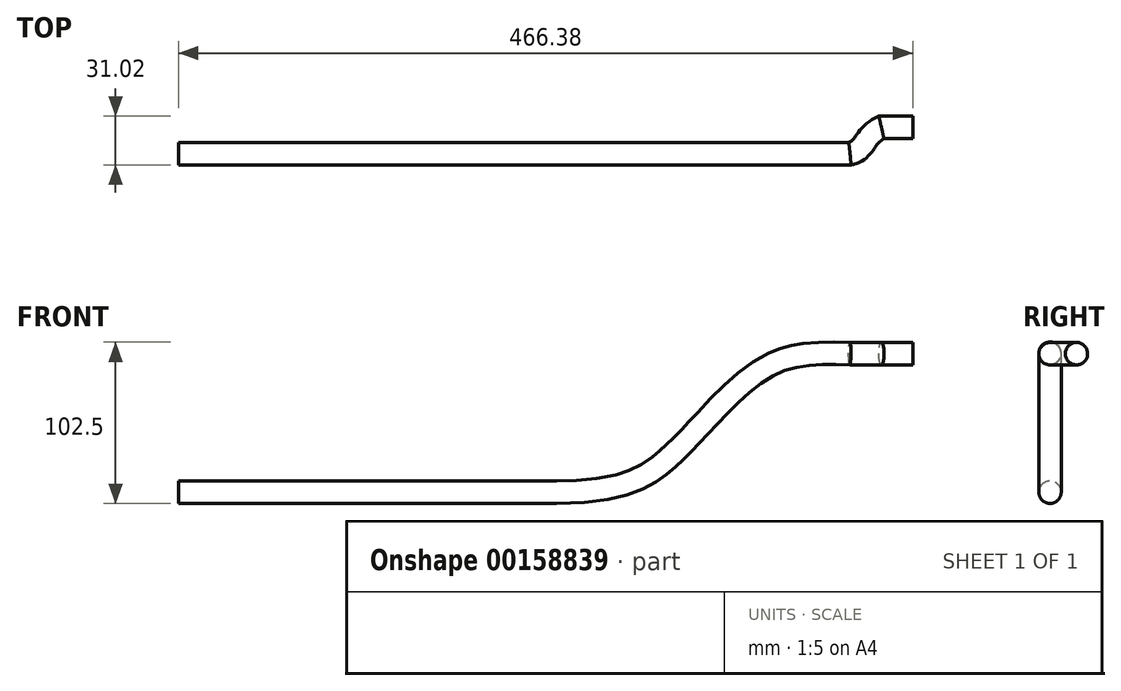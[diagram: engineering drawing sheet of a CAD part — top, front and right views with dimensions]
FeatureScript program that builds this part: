
annotation { "Feature Type Name" : "Feature", "Feature Type Description" : "" }
export const myFeature = defineFeature(function(context is Context, id is Id, definition is map)
    precondition{}
    {
        {
            var Q0;
            Q0=qCreatedBy(makeId("Top.planeOp"),FACE);
            var sketch = newSketch(context, id + "F0", { "sketchPlane" : qUnion([Q0])});
            skLineSegment(sketch, "E0", {"start": v(0, 0) * mm, "end": v(200, 0) * mm});
            skSolve(sketch);
        }
        {
            var Q0;
            Q0=qCreatedBy(makeId("Top.planeOp"),FACE);
            cPlane(context, id + "F1", {"entities" : qUnion([Q0]), "cplaneType" : CPlaneType.OFFSET, "offset" : 88.02 * mm, "width" : 150 * mm, "height" : 150 * mm});
        }
        {
            var Q0;
            Q0=qCreatedBy(makeId("Front.planeOp"),FACE);
            var sketch = newSketch(context, id + "F2", { "sketchPlane" : qUnion([Q0])});
            skPoint(sketch, "E1.0", {"position": v(200, 0) * mm});
            skLineSegment(sketch, "E2", {"start": v(200, 0) * mm, "end": v(466.38, 0) * mm, "construction": true});
            skLineSegment(sketch, "E3", {"start": v(466.38, 0) * mm, "end": v(466.38, 88.02) * mm, "construction": true});
            skLineSegment(sketch, "E4", {"start": v(333.19, 0) * mm, "end": v(333.19, 88.02) * mm, "construction": true});
            skLineSegment(sketch, "E5", {"start": v(200, 0) * mm, "end": v(240, 0) * mm});
            skFitSpline(sketch, "E6", {"points": [v(240, 0) * mm, v(309.55, 20.43) * mm, v(333.19, 44) * mm, v(377.57, 81.87) * mm, v(426.38, 88.02) * mm], "startDerivative": vector(440.48, 0) * mm, "endDerivative": vector(204.36, -6.48) * mm});
            skSolve(sketch);
        }
        {
            var Q0;
            Q0=qCreatedBy(makeId("Right.planeOp"),FACE);
            var sketch = newSketch(context, id + "F3", { "sketchPlane" : qUnion([Q0])});
            skCircle(sketch, "E7", {"center": v(0, 0) * mm, "radius": 7.1 * mm});
            skSolve(sketch);
        }
        {
            var Q0;
            Q0=qCreatedBy(id+"F1.planeOp",FACE);
            var sketch = newSketch(context, id + "F4", { "sketchPlane" : qUnion([Q0])});
            skPoint(sketch, "E8.0", {"position": v(426.38, 0) * mm});
            skLineSegment(sketch, "E9", {"start": v(426.38, 16.82) * mm, "end": v(426.38, 0) * mm, "construction": true});
            skLineSegment(sketch, "E10", {"start": v(426.38, 16.82) * mm, "end": v(466.38, 16.82) * mm, "construction": true});
            skLineSegment(sketch, "E11", {"start": v(446.38, 16.82) * mm, "end": v(466.38, 16.82) * mm});
            skPoint(sketch, "E12.1.internal.snap0", {"position": v(426.38, 8.41) * mm});
            skFitSpline(sketch, "E12", {"points": [v(426.38, 0) * mm, v(436.82, 8.41) * mm, v(446.38, 16.82) * mm], "startDerivative": vector(33.31, 6.31) * mm, "endDerivative": vector(29.76, 14.2) * mm});
            skSolve(sketch);
        }
        {
            var Q0;
            Q0 = qSketchRegion(id + "F3", true);
            var Q1;
            Q1=sQuery(id+"F0.wireOp",EDGE,"E0");
            var Q2;
            Q2=sQuery(id+"F2.wireOp",EDGE,"E5");
            var Q3;
            Q3=sQuery(id+"F2.wireOp",EDGE,"E6");
            var Q4;
            Q4=sQuery(id+"F4.wireOp",EDGE,"2faf410b-5c92-445b-ab43-83f78ee349c2");
            var Q5;
            Q5=sQuery(id+"F4.wireOp",EDGE,"E11");
            var Q6;
            Q6=sQuery(id+"F4.wireOp",EDGE,"E12");
            sweep(context, id + "F5", {"profiles" : qUnion([Q0]), "path" : qUnion([Q1, Q2, Q3, Q4, Q5, Q6])});
        }
    });
